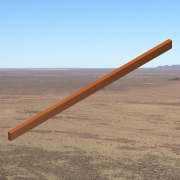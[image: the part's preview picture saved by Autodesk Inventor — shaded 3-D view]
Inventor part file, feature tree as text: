
AUTODESK INVENTOR PART (.ipt)
format: ipt  version: 2014 SP1 (Build 180222100, 222)  size: 126,464 bytes
history: native  units: in
note: dims shown in document units (in); Inventor stores cm internally (conversion verified against a paired STEP export)
features: extrude x1, sketch x1
ambient origin geometry x8: Origin, YZ Plane, XZ Plane, XY Plane, X Axis, Y Axis, Z Axis, Center Point
bodies: Solid1 (feature_tree)
feature tree (2):
  extrude  "Extrusion1"  Depth=3.5in
  sketch  "Sketch2"  dims[d0=1.5in d1=3.5in d2=84.0in d3=0.0in]
